# Revit family: CENTUM Konsole XL120
name_source: partatom
category: HLS-Bauteile
revit_build: Autodesk Revit 2017 (Build: 20190508_0315(x64)
units: mm (PartAtom-declared; Revit-internal decimal feet)

## family parameters
Basisbauteil = Fläche
Beim Laden mit Abzugskörper schneiden = Nein
Bemaßung runder Anschluss = Durchmesser verwenden
Gemeinsam genutzt = Ja
Raumberechnungspunkt = Nein
Teiletyp = Normal

## types (3) — shared parameters
Breite Platte = 220 mm
Breite Profil = 100 mm  [stored 0.328084 ft]
Fabrikat = MEFA
Firma = MEFA Befestigungs- und Montagesysteme GmbH
Höhe Profil = 120 mm
Kurztext1 = Konsole Centum XL 120
Langloch Platte = 27x18 mm
Lochabstand = 150/170 mm
Länge Platte = 240 mm
Material = Stahl
Materialname C-Profil = S235JR
Materialname Platte = S235JR
Oberflaeche = feuerstückverzinkt
Profil = CENTUM
Stärke Platte = 15 mm  [stored 0.0492126 ft]
Stärke Profil = 4 mm  [stored 0.0131234 ft]
Vorgabe-Ansicht = 1219 mm

## per-type parameters (varying)
| type | Artikelnummer | EAN | Gewicht | Gewicht pro Bauteil | Kurztext2 | Länge Konsole | Schienenlänge | max. zul. Last F1 | max. zul. Last F2 | max. zul. Last q0 |
| CENTUM Konsole XL120 L=1440 | 1631201440 | 4250928436825 | 23.96 kg | 23.96 kg | L= 1.440 mm fsv | 1 mm  [stored 0.00328084 ft] | CENTUM Profil XL120 für Konsole_ : CENTUM Profil XL120 L=1440 | 2.81 kip | 1.41 kip | 0.595 kip/ft |
| CENTUM Konsole XL120 L= 960 | 1631200960 | 4250928436818 | 18.10 kg | 18.10 kg | L= 960 mm fsv | 960 mm  [stored 3.14961 ft] | CENTUM Profil XL120 für Konsole_ : CENTUM Profil XL120 L= 960 | 4.22 kip | 2.11 kip | 1.340 kip/ft |
| CENTUM Konsole XL120 L= 720 | 1631200720 | 4250928436801 | 15.17 kg | 15.17 kg | L= 720 mm fsv | 720 mm  [stored 2.3622 ft] | CENTUM Profil XL120 für Konsole_ : CENTUM Profil XL120 L= 720 | 5.62 kip | 2.81 kip | 2.381 kip/ft |

note: [stored X ft] marks values corroborated as IEEE doubles in the binary element streams (Revit-internal decimal feet)
